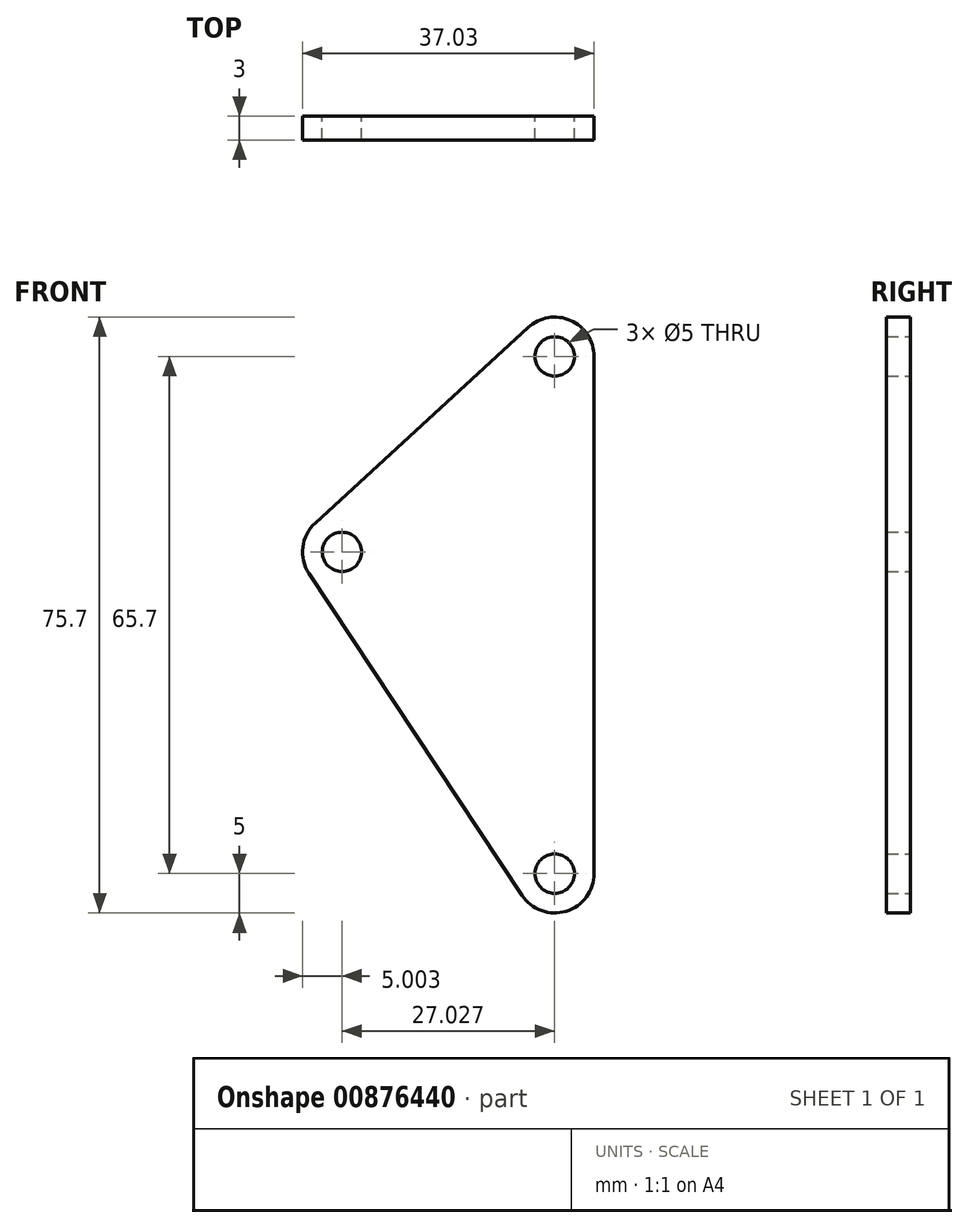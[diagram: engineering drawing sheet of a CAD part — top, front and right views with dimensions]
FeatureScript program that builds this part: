
annotation { "Feature Type Name" : "Feature", "Feature Type Description" : "" }
export const myFeature = defineFeature(function(context is Context, id is Id, definition is map)
    precondition{}
    {
        {
            var Q0;
            Q0=qCreatedBy(makeId("Front.planeOp"),FACE);
            var sketch = newSketch(context, id + "F0", { "sketchPlane" : qUnion([Q0])});
            skLineSegment(sketch, "E0", {"start": v(-4.17, -2.76) * mm, "end": v(-31.2, 38.11) * mm});
            skLineSegment(sketch, "E1", {"start": v(-30.4, 44.55) * mm, "end": v(-3.38, 69.38) * mm});
            skLineSegment(sketch, "E2", {"start": v(5, 65.7) * mm, "end": v(5, 0) * mm});
            skArc(sketch, "E3.filletArc", {"start": v(5, 65.7) * mm, "mid": v(2.01, 70.28) * mm, "end": v(-3.38, 69.38) * mm});
            skArc(sketch, "E4.filletArc", {"start": v(-30.4, 44.55) * mm, "mid": v(-32, 41.48) * mm, "end": v(-31.2, 38.11) * mm});
            skArc(sketch, "E5.filletArc", {"start": v(-4.17, -2.76) * mm, "mid": v(1.44, -4.79) * mm, "end": v(5, 0) * mm});
            skCircle(sketch, "E6", {"center": v(-27.03, 40.87) * mm, "radius": 2.5 * mm});
            skCircle(sketch, "E7", {"center": v(0, 65.7) * mm, "radius": 2.5 * mm});
            skCircle(sketch, "E8", {"center": v(0, 0) * mm, "radius": 2.5 * mm});
            skSolve(sketch);
        }
        {
            var Q0;
            Q0 = qSketchRegion(id + "F0", true);
            extrude(context, id + "F1", {"entities" : qUnion([Q0]), "depth" : 3 * mm, "offsetDistance" : 25 * mm});
        }
    });
